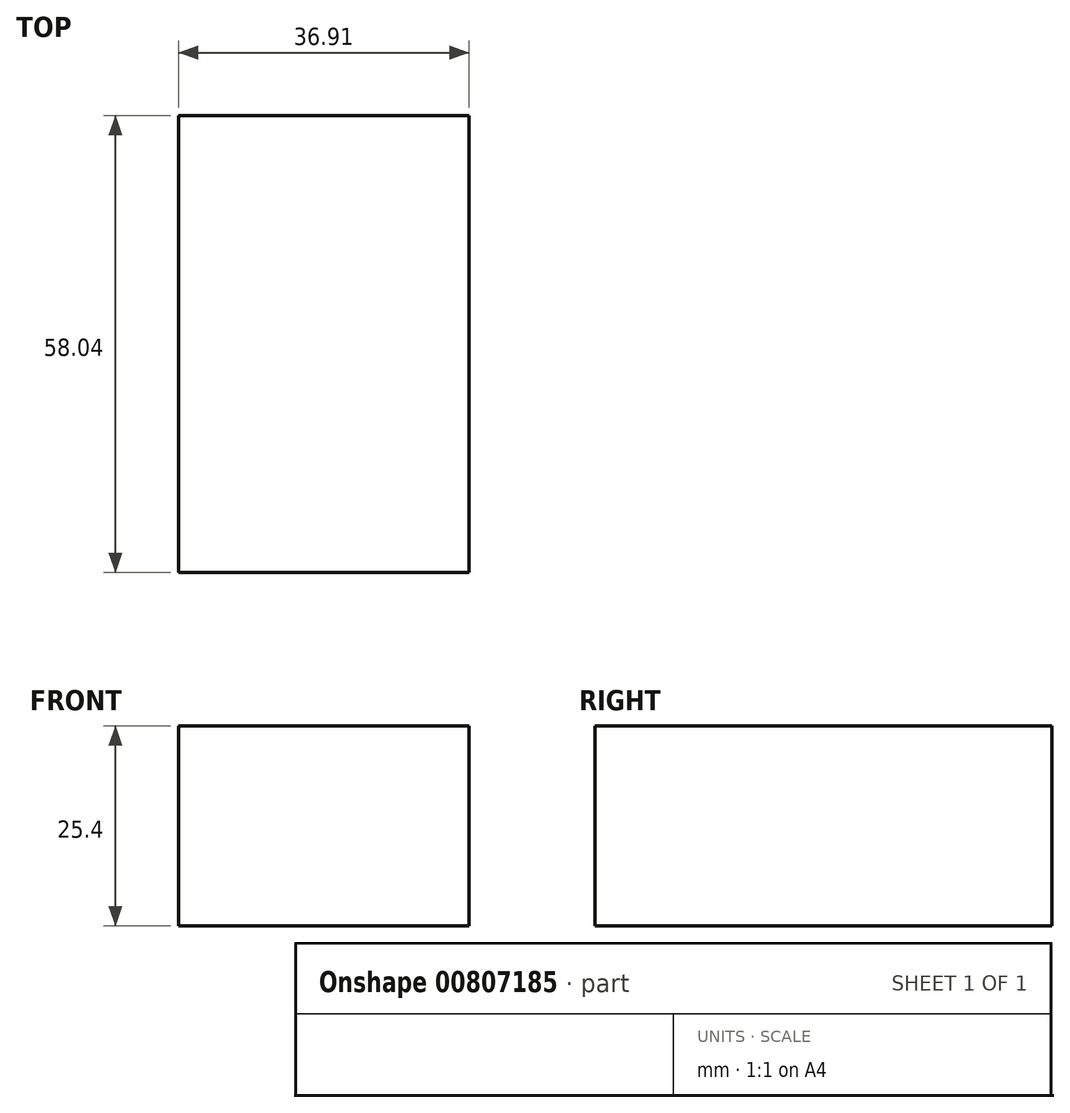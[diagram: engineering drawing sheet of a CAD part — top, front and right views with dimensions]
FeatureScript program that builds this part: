
annotation { "Feature Type Name" : "Feature", "Feature Type Description" : "" }
export const myFeature = defineFeature(function(context is Context, id is Id, definition is map)
    precondition{}
    {
        {
            var Q0;
            Q0=qCreatedBy(makeId("Top.planeOp"),FACE);
            var sketch = newSketch(context, id + "F0", { "sketchPlane" : qUnion([Q0])});
            skLineSegment(sketch, "E0.bottom", {"start": v(-41.05, -30.5) * mm, "end": v(42.46, -30.5) * mm});
            skLineSegment(sketch, "E0.top", {"start": v(-41.05, 29.05) * mm, "end": v(42.46, 29.05) * mm});
            skLineSegment(sketch, "E0.left", {"start": v(-41.05, -30.5) * mm, "end": v(-41.05, 29.05) * mm});
            skLineSegment(sketch, "E0.right", {"start": v(42.46, -30.5) * mm, "end": v(42.46, 29.05) * mm});
            skSolve(sketch);
        }
        {
            var Q0;
            Q0=makeQuery(id+"F0.imprint","IMPRINT",FACE,{"disambiguationData":[TD([[makeQuery(id+"F0.imprint","IMPRINT",EDGE,{"derivedFrom":sQuery(id+"F0.wireOp",EDGE,"E0.bottom")}),1.0]])]});
            var sketch = newSketch(context, id + "F1", { "sketchPlane" : qUnion([Q0])});
            skLineSegment(sketch, "E1.bottom", {"start": v(-19.54, -7.88) * mm, "end": v(-56.45, -7.88) * mm});
            skLineSegment(sketch, "E1.top", {"start": v(-19.54, 50.16) * mm, "end": v(-56.45, 50.16) * mm});
            skLineSegment(sketch, "E1.left", {"start": v(-19.54, -7.88) * mm, "end": v(-19.54, 50.16) * mm});
            skLineSegment(sketch, "E1.right", {"start": v(-56.45, -7.88) * mm, "end": v(-56.45, 50.16) * mm});
            skSolve(sketch);
        }
        {
            var Q0;
            Q0 = qSketchRegion(id + "F1", true);
            extrude(context, id + "F2", {"entities" : qUnion([Q0]), "depth" : 25.4 * mm, "offsetDistance" : 25.4 * mm});
        }
    });
